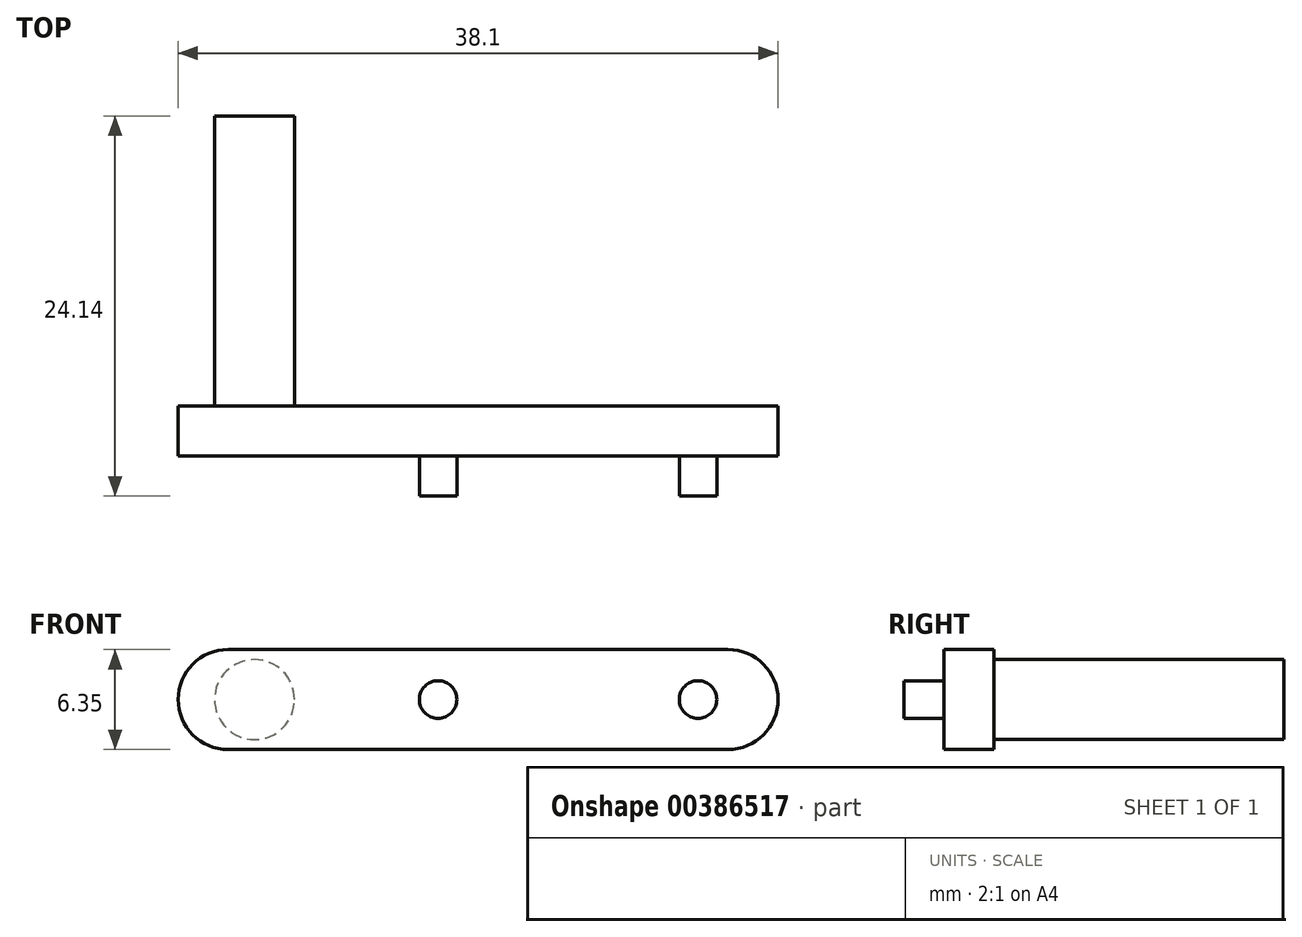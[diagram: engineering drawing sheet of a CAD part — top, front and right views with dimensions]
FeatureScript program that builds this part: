
annotation { "Feature Type Name" : "Feature", "Feature Type Description" : "" }
export const myFeature = defineFeature(function(context is Context, id is Id, definition is map)
    precondition{}
    {
        {
            var Q0;
            Q0=qCreatedBy(makeId("Front.planeOp"),FACE);
            var sketch = newSketch(context, id + "F0", { "sketchPlane" : qUnion([Q0])});
            skLineSegment(sketch, "E0.bottom", {"start": v(0, 0) * mm, "end": v(38.1, 0) * mm});
            skLineSegment(sketch, "E0.top", {"start": v(0, 6.35) * mm, "end": v(38.1, 6.35) * mm});
            skLineSegment(sketch, "E0.left", {"start": v(0, 0) * mm, "end": v(0, 6.35) * mm});
            skLineSegment(sketch, "E0.right", {"start": v(38.1, 0) * mm, "end": v(38.1, 6.35) * mm});
            skSolve(sketch);
        }
        {
            var Q0;
            Q0=makeQuery(id+"F0.imprint","IMPRINT",FACE,{"disambiguationData":[TD([[makeQuery(id+"F0.imprint","IMPRINT",EDGE,{"derivedFrom":sQuery(id+"F0.wireOp",EDGE,"E0.bottom")}),1.0]])]});
            extrude(context, id + "F1", {"entities" : qUnion([Q0]), "depth" : 3.17 * mm});
        }
        {
            var Q0;
            Q0=makeQuery(id+"F1.opExtrude","CAP_FACE",FACE,{"disambiguationData":[OSD([sQuery(id+"F0.wireOp",EDGE,"E0.bottom"),sQuery(id+"F0.wireOp",EDGE,"E0.top"),sQuery(id+"F0.wireOp",EDGE,"E0.left"),sQuery(id+"F0.wireOp",EDGE,"E0.right")])],"isStart":false});
            var sketch = newSketch(context, id + "F2", { "sketchPlane" : qUnion([Q0])});
            skPoint(sketch, "E1", {"position": v(16.51, 3.18) * mm});
            skPoint(sketch, "E2", {"position": v(33.02, 3.18) * mm});
            skCircle(sketch, "E3", {"center": v(16.51, 3.18) * mm, "radius": 1.2 * mm});
            skCircle(sketch, "E4", {"center": v(33.02, 3.18) * mm, "radius": 1.2 * mm});
            skSolve(sketch);
        }
        {
            var Q0;
            Q0 = qSketchRegion(id + "F2", true);
            extrude(context, id + "F3", {"entities" : qUnion([Q0]), "operationType" : NewBodyOperationType.ADD, "depth" : 2.54 * mm});
        }
        {
            var Q0;
            Q0=makeQuery(id+"F1.opExtrude","CAP_FACE",FACE,{"disambiguationData":[OSD([sQuery(id+"F0.wireOp",EDGE,"E0.bottom"),sQuery(id+"F0.wireOp",EDGE,"E0.top"),sQuery(id+"F0.wireOp",EDGE,"E0.left"),sQuery(id+"F0.wireOp",EDGE,"E0.right")])],"isStart":true});
            var sketch = newSketch(context, id + "F4", { "sketchPlane" : qUnion([Q0])});
            skPoint(sketch, "E5", {"position": v(-4.85, 3.18) * mm});
            skCircle(sketch, "E6", {"center": v(-4.85, 3.18) * mm, "radius": 2.54 * mm});
            skSolve(sketch);
        }
        {
            var Q0;
            Q0=makeQuery(id+"F4.imprint","IMPRINT",FACE,{"disambiguationData":[TD([[makeQuery(id+"F4.imprint","IMPRINT",EDGE,{"derivedFrom":sQuery(id+"F4.wireOp",EDGE,"E6")}),1.0]])]});
            extrude(context, id + "F5", {"entities" : qUnion([Q0]), "operationType" : NewBodyOperationType.ADD, "depth" : 18.41 * mm});
        }
        {
            var Q0;
            Q0=makeQuery(id+"F1.opExtrude","SWEPT_EDGE",EDGE,{"disambiguationData":[OSD([sQuery(id+"F0.wireOp",EDGE,"E0.top"),sQuery(id+"F0.wireOp",EDGE,"E0.right")])]});
            var Q1;
            Q1=makeQuery(id+"F1.opExtrude","SWEPT_EDGE",EDGE,{"disambiguationData":[OSD([sQuery(id+"F0.wireOp",EDGE,"E0.bottom"),sQuery(id+"F0.wireOp",EDGE,"E0.right")])]});
            var Q2;
            Q2=makeQuery(id+"F1.opExtrude","SWEPT_EDGE",EDGE,{"disambiguationData":[OSD([sQuery(id+"F0.wireOp",EDGE,"E0.top"),sQuery(id+"F0.wireOp",EDGE,"E0.left")])]});
            var Q3;
            Q3=makeQuery(id+"F1.opExtrude","SWEPT_EDGE",EDGE,{"disambiguationData":[OSD([sQuery(id+"F0.wireOp",EDGE,"E0.bottom"),sQuery(id+"F0.wireOp",EDGE,"E0.left")])]});
            fillet(context, id + "F6", {"entities" : qUnion([Q0, Q1, Q2, Q3]), "radius" : 3.17 * mm, "tangentPropagation" : true, "allowEdgeOverflow" : false});
        }
    });
